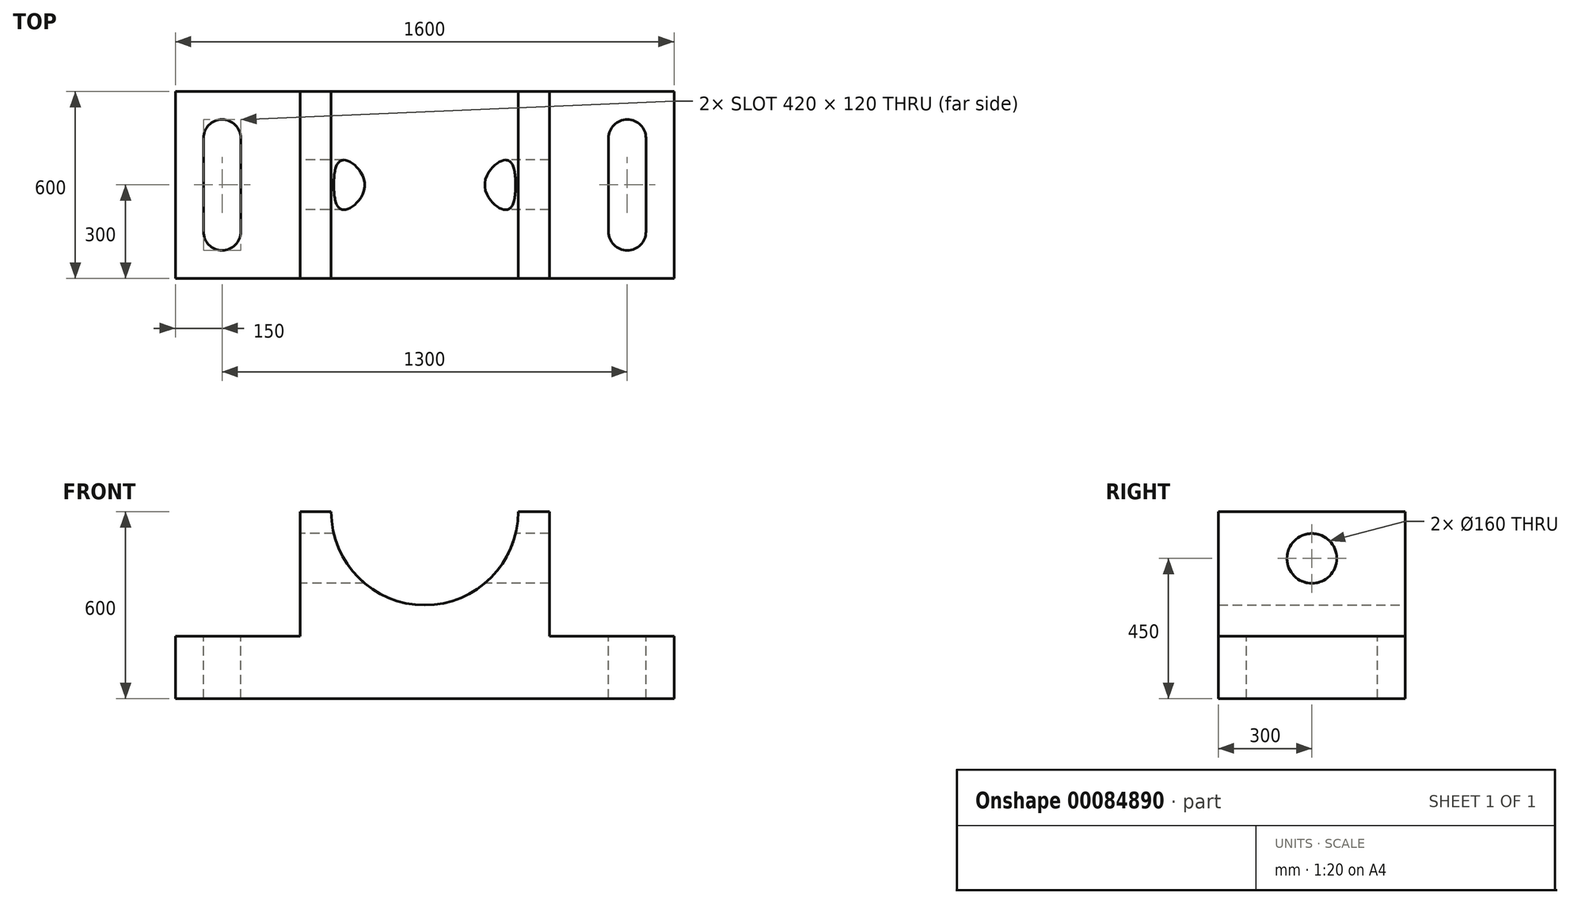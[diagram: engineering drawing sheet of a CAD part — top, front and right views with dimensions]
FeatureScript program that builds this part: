
annotation { "Feature Type Name" : "Feature", "Feature Type Description" : "" }
export const myFeature = defineFeature(function(context is Context, id is Id, definition is map)
    precondition{}
    {
        {
            var Q0;
            Q0=qCreatedBy(makeId("Front.planeOp"),FACE);
            var sketch = newSketch(context, id + "F0", { "sketchPlane" : qUnion([Q0])});
            skLineSegment(sketch, "E0.bottom", {"start": v(-800, -100) * mm, "end": v(800, -100) * mm});
            skLineSegment(sketch, "E0.top", {"start": v(-800, 100) * mm, "end": v(-400, 100) * mm});
            skLineSegment(sketch, "E0.left", {"start": v(-800, -100) * mm, "end": v(-800, 100) * mm});
            skLineSegment(sketch, "E0.right", {"start": v(800, -100) * mm, "end": v(800, 100) * mm});
            skPoint(sketch, "E0.middle", {"position": v(0, 0) * mm});
            skLineSegment(sketch, "E1.bottom", {"start": v(-400, 500) * mm, "end": v(-300, 500) * mm});
            skLineSegment(sketch, "E1.left", {"start": v(-400, 500) * mm, "end": v(-400, 100) * mm});
            skLineSegment(sketch, "E1.right", {"start": v(400, 500) * mm, "end": v(400, 100) * mm});
            skPoint(sketch, "E1.middle", {"position": v(0, 100) * mm});
            skLineSegment(sketch, "E2.trimOffspring", {"start": v(400, 100) * mm, "end": v(800, 100) * mm});
            skPoint(sketch, "E3.trimOffspring.end.orphan", {"position": v(400, -300) * mm});
            skPoint(sketch, "E4.trimOffspring.end.orphan", {"position": v(-400, -300) * mm});
            skArc(sketch, "E5", {"start": v(-300, 500) * mm, "mid": v(0, 200) * mm, "end": v(300, 500) * mm});
            skLineSegment(sketch, "E6.trimOffspring", {"start": v(300, 500) * mm, "end": v(400, 500) * mm});
            skSolve(sketch);
        }
        {
            var Q0;
            Q0 = qSketchRegion(id + "F0", true);
            extrude(context, id + "F1", {"entities" : qUnion([Q0]), "depth" : 600 * mm, "offsetDistance" : 25 * mm});
        }
        {
            var Q0;
            Q0=makeQuery(id+"F1.opExtrude","SWEPT_FACE",FACE,{"disambiguationData":[OSD([sQuery(id+"F0.wireOp",EDGE,"E1.left")])]});
            var sketch = newSketch(context, id + "F2", { "sketchPlane" : qUnion([Q0])});
            skPoint(sketch, "E7.centerSnap0", {"position": v(300, 500) * mm});
            skCircle(sketch, "E8", {"center": v(300, 350) * mm, "radius": 80 * mm});
            skSolve(sketch);
        }
        {
            var Q0;
            Q0 = qSketchRegion(id + "F2", true);
            extrude(context, id + "F3", {"entities" : qUnion([Q0]), "operationType" : NewBodyOperationType.REMOVE, "endBound" : BoundingType.THROUGH_ALL, "oppositeDirection" : true, "depth" : 25 * mm});
        }
        {
            var Q0;
            Q0=makeQuery(id+"F1.opExtrude","SWEPT_FACE",FACE,{"disambiguationData":[OSD([sQuery(id+"F0.wireOp",EDGE,"E2.trimOffspring")])]});
            var sketch = newSketch(context, id + "F4", { "sketchPlane" : qUnion([Q0])});
            skLineSegment(sketch, "E9.left", {"start": v(710, -450) * mm, "end": v(710, -150) * mm});
            skLineSegment(sketch, "E9.right", {"start": v(590, -450) * mm, "end": v(590, -150) * mm});
            skPoint(sketch, "E9.middle", {"position": v(650, -300) * mm});
            skPoint(sketch, "E9.middle.positionSnap0", {"position": v(800, -300) * mm});
            skPoint(sketch, "E9.centerSnap0", {"position": v(800, -300) * mm});
            skArc(sketch, "E10", {"start": v(710, -150) * mm, "mid": v(650, -90) * mm, "end": v(590, -150) * mm});
            skArc(sketch, "E11", {"start": v(590, -450) * mm, "mid": v(650, -510) * mm, "end": v(710, -450) * mm});
            skLineSegment(sketch, "E12.left", {"start": v(-710, -450) * mm, "end": v(-710, -150) * mm});
            skLineSegment(sketch, "E12.right", {"start": v(-590, -450) * mm, "end": v(-590, -150) * mm});
            skPoint(sketch, "E12.middle", {"position": v(-650, -300) * mm});
            skArc(sketch, "E13", {"start": v(-590, -150) * mm, "mid": v(-650, -90) * mm, "end": v(-710, -150) * mm});
            skArc(sketch, "E14", {"start": v(-710, -450) * mm, "mid": v(-650, -510) * mm, "end": v(-590, -450) * mm});
            skSolve(sketch);
        }
        {
            var Q0;
            Q0 = qSketchRegion(id + "F4", true);
            extrude(context, id + "F5", {"entities" : qUnion([Q0]), "operationType" : NewBodyOperationType.REMOVE, "endBound" : BoundingType.THROUGH_ALL, "oppositeDirection" : true, "depth" : 25 * mm});
        }
    });
